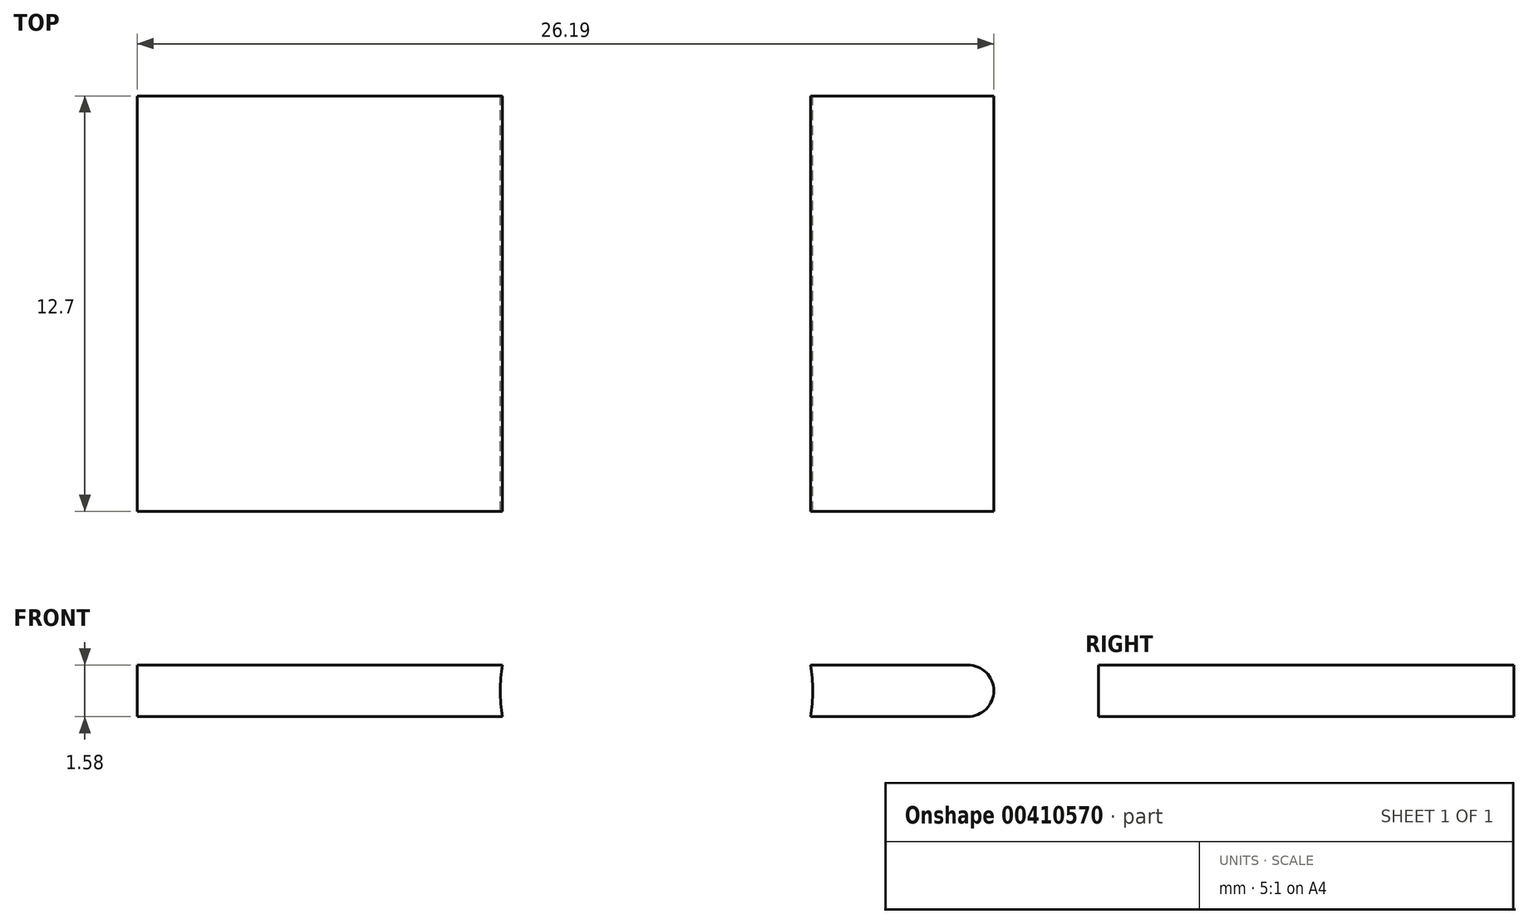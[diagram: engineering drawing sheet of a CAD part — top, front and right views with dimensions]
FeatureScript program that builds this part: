
annotation { "Feature Type Name" : "Feature", "Feature Type Description" : "" }
export const myFeature = defineFeature(function(context is Context, id is Id, definition is map)
    precondition{}
    {
        {
            var Q0;
            Q0=qCreatedBy(makeId("Top.planeOp"),FACE);
            var sketch = newSketch(context, id + "F0", { "sketchPlane" : qUnion([Q0])});
            skLineSegment(sketch, "E0.bottom", {"start": v(0, 0) * mm, "end": v(-63.5, 0) * mm});
            skLineSegment(sketch, "E0.top", {"start": v(0, -12.7) * mm, "end": v(-63.5, -12.7) * mm});
            skLineSegment(sketch, "E0.left", {"start": v(0, 0) * mm, "end": v(0, -12.7) * mm});
            skLineSegment(sketch, "E0.right", {"start": v(-63.5, 0) * mm, "end": v(-63.5, -12.7) * mm});
            skSolve(sketch);
        }
        {
            var Q0;
            Q0=makeQuery(id+"F0.imprint","IMPRINT",FACE,{"disambiguationData":[TD([[makeQuery(id+"F0.imprint","IMPRINT",EDGE,{"derivedFrom":sQuery(id+"F0.wireOp",EDGE,"E0.bottom")}),1.0]])]});
            extrude(context, id + "F1", {"entities" : qUnion([Q0]), "depth" : 25.4 * mm});
        }
        {
            var Q0;
            Q0=makeQuery(id+"F1.opExtrude","SWEPT_FACE",FACE,{"disambiguationData":[OSD([sQuery(id+"F0.wireOp",EDGE,"E0.left")])]});
            var sketch = newSketch(context, id + "F2", { "sketchPlane" : qUnion([Q0])});
            skLineSegment(sketch, "E1", {"start": v(-14.83, 19.81) * mm, "end": v(7.79, 19.81) * mm, "construction": true});
            skLineSegment(sketch, "E2", {"start": v(-14.1, 8.64) * mm, "end": v(9.06, 8.64) * mm, "construction": true});
            skPoint(sketch, "E3", {"position": v(-6.35, 25.4) * mm});
            skPoint(sketch, "E4", {"position": v(-6.35, 0) * mm});
            skLineSegment(sketch, "E5", {"start": v(-6.35, 25.4) * mm, "end": v(-6.35, -8.1) * mm, "construction": true});
            skLineSegment(sketch, "E6", {"start": v(-6.35, -3.71) * mm, "end": v(-6.35, 0) * mm, "construction": true});
            skPoint(sketch, "E7", {"position": v(-6.35, 19.81) * mm});
            skPoint(sketch, "E8", {"position": v(-6.35, 8.64) * mm});
            skSolve(sketch);
        }
        {
            var Q0;
            Q0=sQuery(id+"F2.wireOp",VERTEX,"E7");
            var Q1;
            Q1=makeQuery(id+"F1.opExtrude","SWEPT_BODY",BODY,{"disambiguationData":[OSD([sQuery(id+"F0.wireOp",EDGE,"E0.bottom"),sQuery(id+"F0.wireOp",EDGE,"E0.top"),sQuery(id+"F0.wireOp",EDGE,"E0.left"),sQuery(id+"F0.wireOp",EDGE,"E0.right")])]});
            hole(context, id + "F3", {"style" : HoleStyle.SIMPLE, "endStyle" : HoleEndStyle.BLIND, "standardTappedOrClearance" : lookupTablePath({ "standard" : "ANSI", "engagement" : "75%", "pitch" : "24 tpi", "size" : "#10", "type" : "Tapped" }), "standardBlindInLast" : lookupTablePath({ "standard" : "ANSI", "engagement" : "75%", "pitch" : "24 tpi", "size" : "#10", "type" : "Tapped" }), "holeDiameter" : 3.8 * mm, "showTappedDepth" : true, "holeDepth" : 12.7 * mm, "isTappedThrough" : true, "tappedDepth" : 9.52 * mm, "tapClearance" : 3, "startFromSketch" : true, "locations" : qUnion([Q0]), "scope" : qUnion([Q1]), "majorDiameter" : 4.83 * mm});
        }
        {
            var Q0;
            Q0=sQuery(id+"F2.wireOp",VERTEX,"E8");
            var Q1;
            Q1=makeQuery(id+"F1.opExtrude","SWEPT_BODY",BODY,{"disambiguationData":[OSD([sQuery(id+"F0.wireOp",EDGE,"E0.bottom"),sQuery(id+"F0.wireOp",EDGE,"E0.top"),sQuery(id+"F0.wireOp",EDGE,"E0.left"),sQuery(id+"F0.wireOp",EDGE,"E0.right")])]});
            hole(context, id + "F4", {"style" : HoleStyle.SIMPLE, "endStyle" : HoleEndStyle.BLIND, "standardTappedOrClearance" : lookupTablePath({ "standard" : "ANSI", "engagement" : "75%", "pitch" : "24 tpi", "size" : "#10", "type" : "Tapped" }), "standardBlindInLast" : lookupTablePath({ "standard" : "ANSI", "engagement" : "75%", "pitch" : "24 tpi", "size" : "#10", "type" : "Tapped" }), "holeDiameter" : 3.8 * mm, "showTappedDepth" : true, "holeDepth" : 12.7 * mm, "isTappedThrough" : true, "tappedDepth" : 9.52 * mm, "tapClearance" : 3, "startFromSketch" : true, "locations" : qUnion([Q0]), "scope" : qUnion([Q1]), "majorDiameter" : 4.83 * mm});
        }
        {
            var Q0;
            Q0=makeQuery(id+"F1.opExtrude","SWEPT_FACE",FACE,{"disambiguationData":[OSD([sQuery(id+"F0.wireOp",EDGE,"E0.bottom")])]});
            var sketch = newSketch(context, id + "F5", { "sketchPlane" : qUnion([Q0])});
            skPoint(sketch, "E9", {"position": v(0, 12.7) * mm});
            skPoint(sketch, "E10", {"position": v(63.5, 12.7) * mm});
            skLineSegment(sketch, "E11", {"start": v(38.1, 12.7) * mm, "end": v(65.23, 12.7) * mm});
            skLineSegment(sketch, "E12", {"start": v(47.62, 27.3) * mm, "end": v(47.62, -3.25) * mm, "construction": true});
            skPoint(sketch, "E13", {"position": v(47.62, 12.7) * mm});
            skLineSegment(sketch, "E14", {"start": v(38.1, 22.23) * mm, "end": v(38.1, -3.17) * mm, "construction": true});
            skPoint(sketch, "E15", {"position": v(38.1, 12.7) * mm});
            skArc(sketch, "E16.0.startCap", {"start": v(38.1, 11.91) * mm, "mid": v(37.31, 12.7) * mm, "end": v(38.1, 13.49) * mm});
            skArc(sketch, "E16.0.endCap", {"start": v(65.23, 13.49) * mm, "mid": v(66.01, 12.7) * mm, "end": v(65.23, 11.91) * mm});
            skLineSegment(sketch, "E16.0.left", {"start": v(38.1, 13.49) * mm, "end": v(65.23, 13.49) * mm});
            skLineSegment(sketch, "E16.0.right", {"start": v(38.1, 11.91) * mm, "end": v(65.23, 11.91) * mm});
            skPoint(sketch, "E17", {"position": v(47.62, 0) * mm});
            skPoint(sketch, "E18", {"position": v(63.5, 0) * mm});
            skSolve(sketch);
        }
        {
            var Q0;
            Q0=sQuery(id+"F5.wireOp",VERTEX,"E13");
            var Q1;
            Q1=makeQuery(id+"F1.opExtrude","SWEPT_BODY",BODY,{"disambiguationData":[OSD([sQuery(id+"F0.wireOp",EDGE,"E0.bottom"),sQuery(id+"F0.wireOp",EDGE,"E0.top"),sQuery(id+"F0.wireOp",EDGE,"E0.left"),sQuery(id+"F0.wireOp",EDGE,"E0.right")])]});
            hole(context, id + "F6", {"style" : HoleStyle.SIMPLE, "endStyle" : HoleEndStyle.THROUGH, "holeDiameter" : 9.55 * mm, "isTappedThrough" : true, "tappedDepth" : 9.52 * mm, "tapClearance" : 3, "startFromSketch" : true, "locations" : qUnion([Q0]), "scope" : qUnion([Q1])});
        }
        {
            var Q0;
            {var subQ4=sQuery(id+"F5.wireOp",EDGE,"E16.0.startCap");Q0=makeQuery(id+"F5.imprint","IMPRINT",FACE,{"disambiguationData":[TD([[makeQuery(id+"F5.imprint","IMPRINT",EDGE,{"derivedFrom":subQ4}),-1.0]])]});}
            extrude(context, id + "F7", {"entities" : qUnion([Q0]), "operationType" : NewBodyOperationType.REMOVE, "endBound" : BoundingType.THROUGH_ALL, "oppositeDirection" : true, "depth" : 25.4 * mm});
        }
        {
            var Q0;
            Q0=makeQuery(id+"F1.opExtrude","SWEPT_FACE",FACE,{"disambiguationData":[OSD([sQuery(id+"F0.wireOp",EDGE,"E0.top")])]});
            var sketch = newSketch(context, id + "F8", { "sketchPlane" : qUnion([Q0])});
            skPoint(sketch, "E19", {"position": v(-52.33, 11.91) * mm});
            skPoint(sketch, "E20", {"position": v(-63.5, 11.91) * mm});
            skPoint(sketch, "E21", {"position": v(-57.92, 11.91) * mm});
            skLineSegment(sketch, "E22", {"start": v(-57.92, 12.17) * mm, "end": v(-57.92, -2.15) * mm, "construction": true});
            skLineSegment(sketch, "E23", {"start": v(-57.92, 12.17) * mm, "end": v(-57.92, 26.68) * mm, "construction": true});
            skPoint(sketch, "E24", {"position": v(-57.92, 13.49) * mm});
            skSolve(sketch);
        }
        {
            var Q0;
            Q0=makeQuery(id+"F7.boolean.opBoolean","COPY",FACE,{"disambiguationData":[TD([makeQuery(id+"F1.opExtrude","SWEPT_FACE",FACE,{"disambiguationData":[OSD([sQuery(id+"F0.wireOp",EDGE,"E0.right")])]})])],"derivedFrom":makeQuery(id+"F7.opExtrude","SWEPT_FACE",FACE,{"disambiguationData":[OSD([sQuery(id+"F5.wireOp",EDGE,"E16.0.right")])]})});
            var sketch = newSketch(context, id + "F9", { "sketchPlane" : qUnion([Q0])});
            skLineSegment(sketch, "E25", {"start": v(-57.92, -12.7) * mm, "end": v(-57.92, -5.12) * mm, "construction": true});
            skPoint(sketch, "E26", {"position": v(-57.92, -6.35) * mm});
            skSolve(sketch);
        }
        {
            var Q0;
            Q0=sQuery(id+"F9.wireOp",VERTEX,"E26");
            var Q1;
            Q1=makeQuery(id+"F1.opExtrude","SWEPT_BODY",BODY,{"disambiguationData":[OSD([sQuery(id+"F0.wireOp",EDGE,"E0.bottom"),sQuery(id+"F0.wireOp",EDGE,"E0.top"),sQuery(id+"F0.wireOp",EDGE,"E0.left"),sQuery(id+"F0.wireOp",EDGE,"E0.right")])]});
            hole(context, id + "F10", {"style" : HoleStyle.SIMPLE, "endStyle" : HoleEndStyle.THROUGH, "standardTappedOrClearance" : lookupTablePath({ "standard" : "ISO", "fit" : "Normal", "size" : "M5", "type" : "Clearance" }), "standardBlindInLast" : lookupTablePath({ "fit" : "Standard", "standard" : "ISO", "size" : "M5", "type" : "Clearance" }), "holeDiameter" : 5.5 * mm, "isTappedThrough" : true, "tappedDepth" : 9.52 * mm, "tapClearance" : 3, "startFromSketch" : true, "locations" : qUnion([Q0]), "scope" : qUnion([Q1])});
        }
        {
            var Q0;
            Q0=makeQuery(id+"F7.boolean.opBoolean","COPY",FACE,{"disambiguationData":[TD([makeQuery(id+"F1.opExtrude","SWEPT_FACE",FACE,{"disambiguationData":[OSD([sQuery(id+"F0.wireOp",EDGE,"E0.right")])]})])],"derivedFrom":makeQuery(id+"F7.opExtrude","SWEPT_FACE",FACE,{"disambiguationData":[OSD([sQuery(id+"F5.wireOp",EDGE,"E16.0.left")])]})});
            var sketch = newSketch(context, id + "F11", { "sketchPlane" : qUnion([Q0])});
            skLineSegment(sketch, "E27", {"start": v(-57.92, 12.7) * mm, "end": v(-57.86, 0) * mm, "construction": true});
            skPoint(sketch, "E28", {"position": v(-57.89, 6.35) * mm});
            skSolve(sketch);
        }
        {
            var Q0;
            Q0=sQuery(id+"F11.wireOp",VERTEX,"E28");
            var Q1;
            Q1=makeQuery(id+"F1.opExtrude","SWEPT_BODY",BODY,{"disambiguationData":[OSD([sQuery(id+"F0.wireOp",EDGE,"E0.bottom"),sQuery(id+"F0.wireOp",EDGE,"E0.top"),sQuery(id+"F0.wireOp",EDGE,"E0.left"),sQuery(id+"F0.wireOp",EDGE,"E0.right")])]});
            hole(context, id + "F12", {"style" : HoleStyle.SIMPLE, "endStyle" : HoleEndStyle.THROUGH, "standardTappedOrClearance" : lookupTablePath({ "standard" : "ISO", "engagement" : "75%", "pitch" : "0.8 mm", "size" : "M5", "type" : "Tapped" }), "standardBlindInLast" : lookupTablePath({ "standard" : "ISO", "engagement" : "75%", "pitch" : "0.8 mm", "size" : "M5", "type" : "Tapped" }), "holeDiameter" : 4.2 * mm, "showTappedDepth" : true, "isTappedThrough" : true, "tappedDepth" : 9.52 * mm, "tapClearance" : 3, "startFromSketch" : true, "locations" : qUnion([Q0]), "scope" : qUnion([Q1]), "majorDiameter" : 5 * mm});
        }
    });
